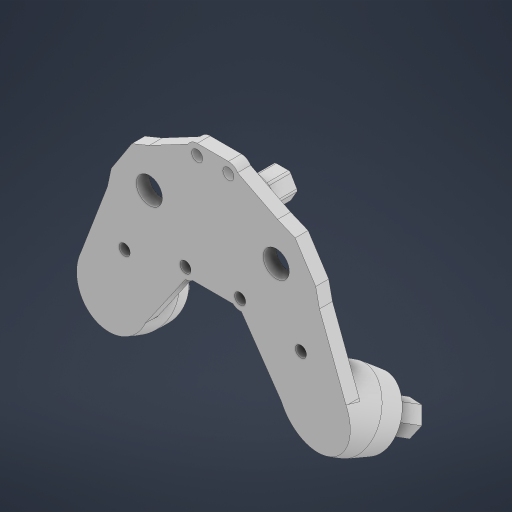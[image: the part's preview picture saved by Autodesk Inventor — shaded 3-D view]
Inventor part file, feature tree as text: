
AUTODESK INVENTOR PART (.ipt)
format: ipt  version: 2024 (Build 280153000, 153)  size: 355,840 bytes
history: native  units: in
note: dims shown in document units (in); Inventor stores cm internally (conversion verified against a paired STEP export)
features: other x9, reference x7, sketch x6, extrude x6, plane x3, chamfer x3, fillet x1, mirror x1
ambient origin geometry x8: Origin, YZ Plane, XZ Plane, XY Plane, X Axis, Y Axis, Z Axis, Center Point
bodies: Solid1 (feature_tree)
feature tree (36):
  sketch  "Sketch1"  dims[d0=0.3976in d1=1.0in d2=0.0in]
  plane  "Work Plane1"
  extrude  "Extrusion1"  Depth=1.0in TaperAngle=0.0deg
  extrude  "Extrusion3"  Depth=0.3976in
  plane  "Work Plane2"
  sketch  "Sketch5"  dims[d14=0.315in d15=0.0in d16=0.0394in d17=1.0in d18=0.0in]
  plane  "Work Plane3"
  extrude  "Extrusion4"  Depth=0.0394in
  fillet  "Fillet1"  Radius=1.0in
  extrude  "Extrusion5"  Depth=0.1969in
  chamfer  "Chamfer3"  Distance=0.1969in
  chamfer  "Chamfer4"  Distance=0.0787in
  chamfer  "Chamfer5"  Distance=0.0787in
  mirror  "Mirror1"
  extrude  "Extrusion6"  Depth=0.3937in
  extrude  "Extrusion7"  Depth=0.1969in TaperAngle=0.0deg
  reference  "Reference1"
  sketch  "Sketch3"  dims[d8=0.4331in d9=0.0in d13=0.3976in]
  reference  "Reference6"
  reference  "Reference8"
  sketch  "Sketch6"  dims[d19=0.0787in d20=0.125in d21=0.5497in d22=0.1083in d23=0.125in d24=0.5497in d25=0.1969in d26=0.125in d27=0.5497in]
  reference  "Reference9"
  reference  "Reference10"
  reference  "Reference11"
  sketch  "Sketch7"  dims[d28=0.0787in]
  reference  "Reference12"
  sketch  "Sketch8"  dims[d29=0.0787in d30=0.0787in d31=0.0787in d32=0.0787in d33=0.1969in d34=0.0in d35=0.4331in d36=0.0in d37=0.3937in d38=0.3937in]
  other  "<userpath>\Desktop\SeniorDesign\Head_V3\Robot_Head_Neck_Assembly.iam"
  other  "Robot_Head_Neck_Assembly.iam"
  other  "Neck_Cover_United:1"
  other  "Universal_Joint:1"
  other  "Universal_Joint_Connector:2"
  other  "Universal_Joint_Connector:3"
  other  "Head_V3_Assembly:1"
  other  "Head_base_mount:1"
  other  "Assembly1"
